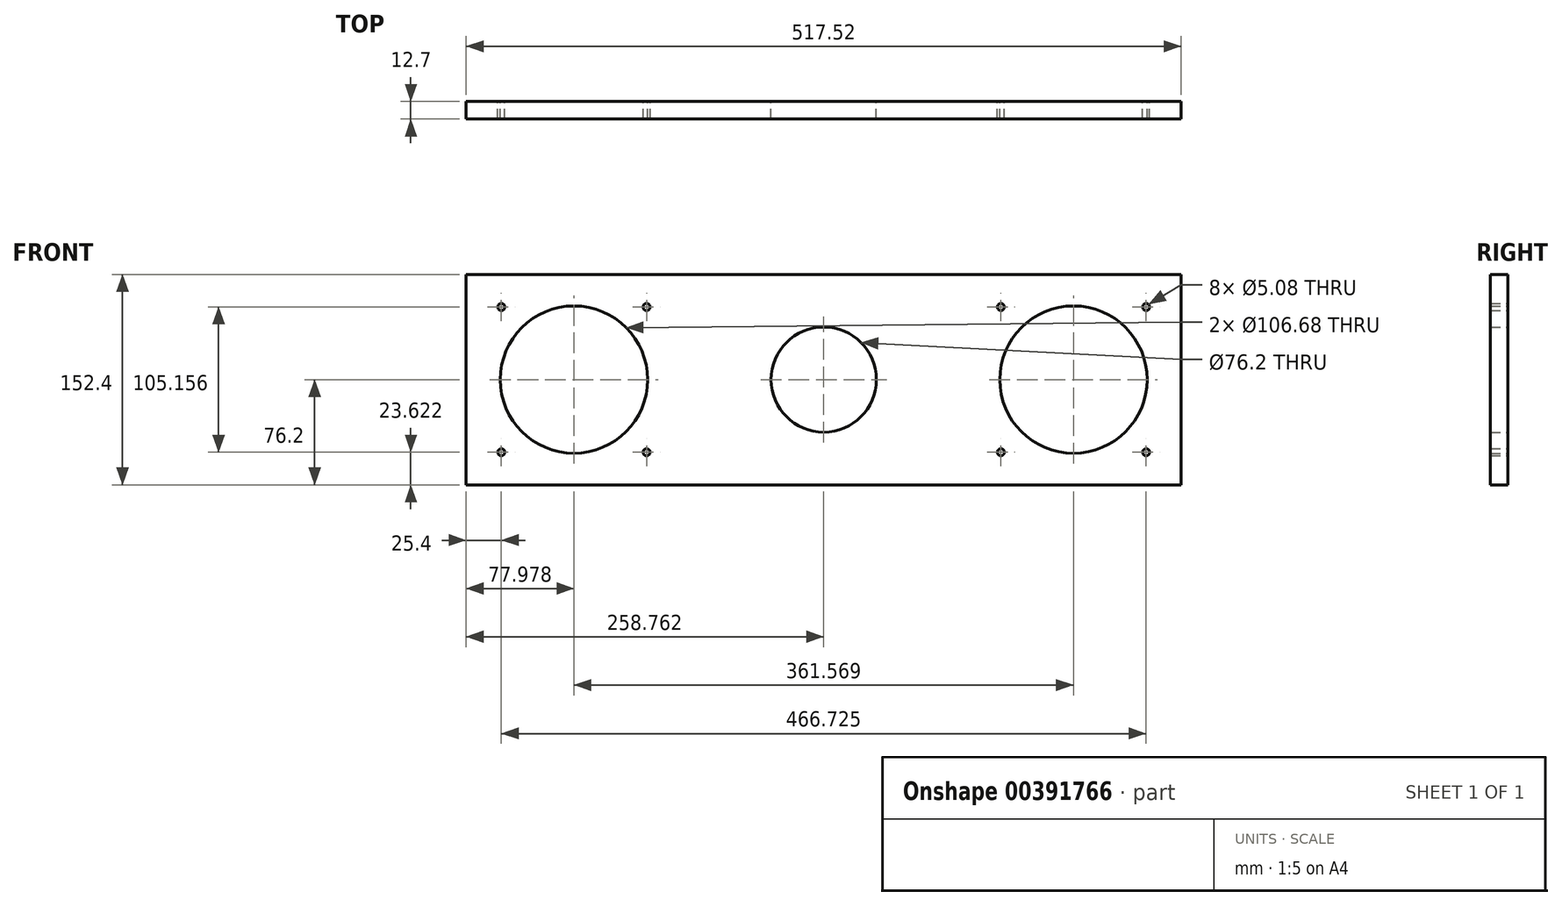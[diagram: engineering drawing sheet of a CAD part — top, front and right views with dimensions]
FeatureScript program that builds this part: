
annotation { "Feature Type Name" : "Feature", "Feature Type Description" : "" }
export const myFeature = defineFeature(function(context is Context, id is Id, definition is map)
    precondition{}
    {
        {
            var Q0;
            Q0=qCreatedBy(makeId("Front.planeOp"),FACE);
            var sketch = newSketch(context, id + "F0", { "sketchPlane" : qUnion([Q0])});
            skLineSegment(sketch, "E0.bottom", {"start": v(0, 0) * mm, "end": v(517.52, 0) * mm});
            skLineSegment(sketch, "E0.top", {"start": v(0, 152.4) * mm, "end": v(517.52, 152.4) * mm});
            skLineSegment(sketch, "E0.left", {"start": v(0, 0) * mm, "end": v(0, 152.4) * mm});
            skLineSegment(sketch, "E0.right", {"start": v(517.52, 0) * mm, "end": v(517.52, 152.4) * mm});
            skCircle(sketch, "E1", {"center": v(77.98, 76.2) * mm, "radius": 53.34 * mm});
            skCircle(sketch, "E2", {"center": v(439.55, 76.2) * mm, "radius": 53.34 * mm});
            skCircle(sketch, "E3", {"center": v(130.56, 128.78) * mm, "radius": 2.54 * mm});
            skCircle(sketch, "E4", {"center": v(25.4, 128.78) * mm, "radius": 2.54 * mm});
            skCircle(sketch, "E5", {"center": v(25.4, 23.62) * mm, "radius": 2.54 * mm});
            skCircle(sketch, "E6", {"center": v(130.56, 23.62) * mm, "radius": 2.54 * mm});
            skCircle(sketch, "E7", {"center": v(386.97, 128.78) * mm, "radius": 2.54 * mm});
            skCircle(sketch, "E8", {"center": v(492.13, 128.78) * mm, "radius": 2.54 * mm});
            skCircle(sketch, "E9", {"center": v(492.13, 23.62) * mm, "radius": 2.54 * mm});
            skCircle(sketch, "E10", {"center": v(386.97, 23.62) * mm, "radius": 2.54 * mm});
            skCircle(sketch, "E11", {"center": v(258.76, 76.2) * mm, "radius": 38.1 * mm});
            skSolve(sketch);
        }
        {
            var Q0;
            Q0 = qSketchRegion(id + "F0", true);
            extrude(context, id + "F1", {"entities" : qUnion([Q0]), "depth" : 12.7 * mm});
        }
    });
